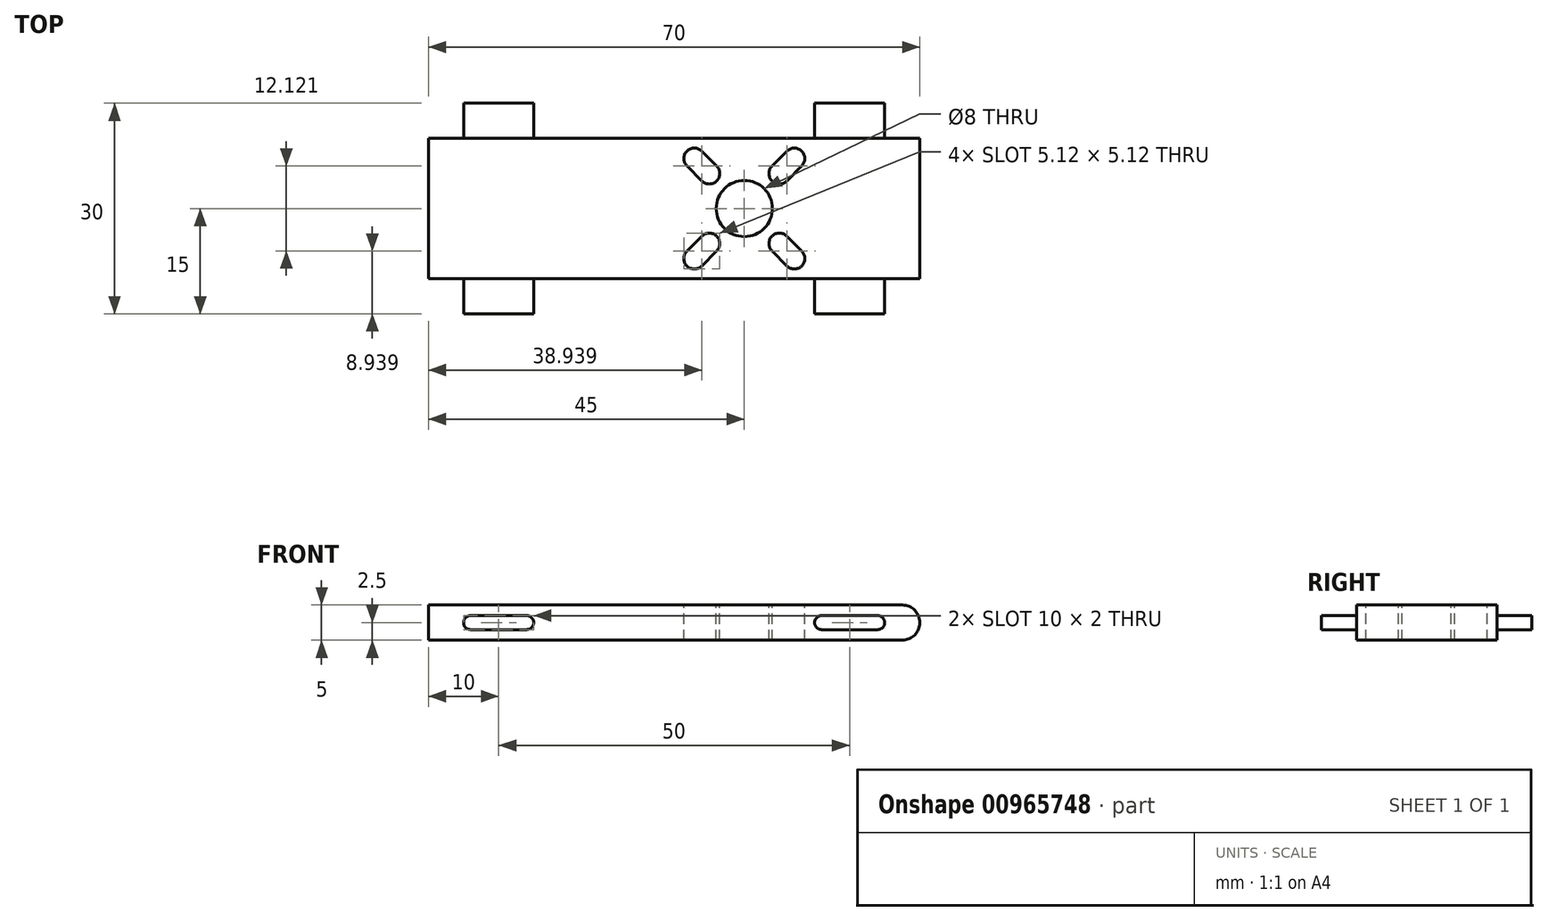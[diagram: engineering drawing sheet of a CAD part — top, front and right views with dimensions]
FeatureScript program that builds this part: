
annotation { "Feature Type Name" : "Feature", "Feature Type Description" : "" }
export const myFeature = defineFeature(function(context is Context, id is Id, definition is map)
    precondition{}
    {
        {
            var Q0;
            Q0=qCreatedBy(makeId("Top.planeOp"),FACE);
            var sketch = newSketch(context, id + "F0", { "sketchPlane" : qUnion([Q0])});
            skLineSegment(sketch, "E0.bottom", {"start": v(35, 10) * mm, "end": v(-35, 10) * mm});
            skLineSegment(sketch, "E0.top", {"start": v(35, -10) * mm, "end": v(-35, -10) * mm});
            skLineSegment(sketch, "E0.left", {"start": v(35, 10) * mm, "end": v(35, -10) * mm});
            skLineSegment(sketch, "E0.right", {"start": v(-35, 10) * mm, "end": v(-35, -10) * mm});
            skPoint(sketch, "E0.middle", {"position": v(0, 0) * mm});
            skSolve(sketch);
        }
        {
            var Q0;
            Q0=makeQuery(id+"F0.imprint","IMPRINT",FACE,{"disambiguationData":[TD([[makeQuery(id+"F0.imprint","IMPRINT",EDGE,{"derivedFrom":sQuery(id+"F0.wireOp",EDGE,"E0.bottom")}),1.0]])]});
            extrude(context, id + "F1", {"entities" : qUnion([Q0]), "depth" : 5 * mm, "offsetDistance" : 25 * mm});
        }
        {
            var Q0;
            Q0=makeQuery(id+"F1.opExtrude","SWEPT_FACE",FACE,{"disambiguationData":[OSD([sQuery(id+"F0.wireOp",EDGE,"E0.top")])]});
            var sketch = newSketch(context, id + "F2", { "sketchPlane" : qUnion([Q0])});
            skLineSegment(sketch, "E1.bottom", {"start": v(-20, 1.5) * mm, "end": v(-30, 1.5) * mm});
            skLineSegment(sketch, "E1.top", {"start": v(-20, 3.5) * mm, "end": v(-30, 3.5) * mm});
            skLineSegment(sketch, "E1.left", {"start": v(-20, 1.5) * mm, "end": v(-20, 3.5) * mm});
            skLineSegment(sketch, "E1.right", {"start": v(-30, 1.5) * mm, "end": v(-30, 3.5) * mm});
            skPoint(sketch, "E1.middle", {"position": v(-25, 2.5) * mm});
            skLineSegment(sketch, "E2.bottom", {"start": v(30, 1.5) * mm, "end": v(20, 1.5) * mm});
            skLineSegment(sketch, "E2.top", {"start": v(30, 3.5) * mm, "end": v(20, 3.5) * mm});
            skLineSegment(sketch, "E2.left", {"start": v(30, 1.5) * mm, "end": v(30, 3.5) * mm});
            skLineSegment(sketch, "E2.right", {"start": v(20, 1.5) * mm, "end": v(20, 3.5) * mm});
            skPoint(sketch, "E3.end.orphan", {"position": v(-35, 5) * mm});
            skPoint(sketch, "E4.start.orphan", {"position": v(35, 5) * mm});
            skSolve(sketch);
        }
        {
            var Q0;
            Q0 = qSketchRegion(id + "F2", true);
            extrude(context, id + "F3", {"entities" : qUnion([Q0]), "operationType" : NewBodyOperationType.ADD, "depth" : 5 * mm, "offsetDistance" : 25 * mm});
        }
        {
            var Q0;
            Q0=makeQuery(id+"F1.opExtrude","SWEPT_FACE",FACE,{"disambiguationData":[OSD([sQuery(id+"F0.wireOp",EDGE,"E0.bottom")])]});
            var sketch = newSketch(context, id + "F4", { "sketchPlane" : qUnion([Q0])});
            skLineSegment(sketch, "E5.bottom", {"start": v(-20, 3.5) * mm, "end": v(-30, 3.5) * mm});
            skLineSegment(sketch, "E5.top", {"start": v(-20, 1.5) * mm, "end": v(-30, 1.5) * mm});
            skLineSegment(sketch, "E5.left", {"start": v(-20, 3.5) * mm, "end": v(-20, 1.5) * mm});
            skLineSegment(sketch, "E5.right", {"start": v(-30, 3.5) * mm, "end": v(-30, 1.5) * mm});
            skPoint(sketch, "E5.middle", {"position": v(-25, 2.5) * mm});
            skLineSegment(sketch, "E6.bottom", {"start": v(30, 1.5) * mm, "end": v(20, 1.5) * mm});
            skLineSegment(sketch, "E6.top", {"start": v(30, 3.5) * mm, "end": v(20, 3.5) * mm});
            skLineSegment(sketch, "E6.left", {"start": v(30, 1.5) * mm, "end": v(30, 3.5) * mm});
            skLineSegment(sketch, "E6.right", {"start": v(20, 1.5) * mm, "end": v(20, 3.5) * mm});
            skPoint(sketch, "E6.middle", {"position": v(25, 2.5) * mm});
            skSolve(sketch);
        }
        {
            var Q0;
            Q0 = qSketchRegion(id + "F4", true);
            extrude(context, id + "F5", {"entities" : qUnion([Q0]), "operationType" : NewBodyOperationType.ADD, "depth" : 5 * mm, "offsetDistance" : 25 * mm});
        }
        {
            var Q0;
            Q0=makeQuery(id+"F5.opExtrude","SWEPT_EDGE",EDGE,{"disambiguationData":[OSD([sQuery(id+"F4.wireOp",EDGE,"E5.bottom"),sQuery(id+"F4.wireOp",EDGE,"E5.right")])]});
            var Q1;
            Q1=makeQuery(id+"F5.opExtrude","SWEPT_EDGE",EDGE,{"disambiguationData":[OSD([sQuery(id+"F4.wireOp",EDGE,"E5.top"),sQuery(id+"F4.wireOp",EDGE,"E5.right")])]});
            var Q2;
            Q2=makeQuery(id+"F5.opExtrude","SWEPT_EDGE",EDGE,{"disambiguationData":[OSD([sQuery(id+"F4.wireOp",EDGE,"E5.bottom"),sQuery(id+"F4.wireOp",EDGE,"E5.left")])]});
            var Q3;
            Q3=makeQuery(id+"F3.opExtrude","SWEPT_EDGE",EDGE,{"disambiguationData":[OSD([sQuery(id+"F2.wireOp",EDGE,"E2.top"),sQuery(id+"F2.wireOp",EDGE,"E2.left")])]});
            var Q4;
            Q4=makeQuery(id+"F3.opExtrude","SWEPT_EDGE",EDGE,{"disambiguationData":[OSD([sQuery(id+"F2.wireOp",EDGE,"E2.bottom"),sQuery(id+"F2.wireOp",EDGE,"E2.left")])]});
            var Q5;
            Q5=makeQuery(id+"F3.opExtrude","SWEPT_EDGE",EDGE,{"disambiguationData":[OSD([sQuery(id+"F2.wireOp",EDGE,"E2.top"),sQuery(id+"F2.wireOp",EDGE,"E2.right")])]});
            var Q6;
            Q6=makeQuery(id+"F5.opExtrude","SWEPT_EDGE",EDGE,{"disambiguationData":[OSD([sQuery(id+"F4.wireOp",EDGE,"E6.top"),sQuery(id+"F4.wireOp",EDGE,"E6.right")])]});
            var Q7;
            Q7=makeQuery(id+"F5.opExtrude","SWEPT_EDGE",EDGE,{"disambiguationData":[OSD([sQuery(id+"F4.wireOp",EDGE,"E6.bottom"),sQuery(id+"F4.wireOp",EDGE,"E6.right")])]});
            var Q8;
            Q8=makeQuery(id+"F3.opExtrude","SWEPT_EDGE",EDGE,{"disambiguationData":[OSD([sQuery(id+"F2.wireOp",EDGE,"E1.top"),sQuery(id+"F2.wireOp",EDGE,"E1.right")])]});
            var Q9;
            Q9=makeQuery(id+"F3.opExtrude","SWEPT_EDGE",EDGE,{"disambiguationData":[OSD([sQuery(id+"F2.wireOp",EDGE,"E1.top"),sQuery(id+"F2.wireOp",EDGE,"E1.left")])]});
            var Q10;
            Q10=makeQuery(id+"F3.opExtrude","SWEPT_EDGE",EDGE,{"disambiguationData":[OSD([sQuery(id+"F2.wireOp",EDGE,"E1.bottom"),sQuery(id+"F2.wireOp",EDGE,"E1.left")])]});
            var Q11;
            Q11=makeQuery(id+"F5.opExtrude","SWEPT_EDGE",EDGE,{"disambiguationData":[OSD([sQuery(id+"F4.wireOp",EDGE,"E6.top"),sQuery(id+"F4.wireOp",EDGE,"E6.left")])]});
            var Q12;
            Q12=makeQuery(id+"F5.opExtrude","SWEPT_EDGE",EDGE,{"disambiguationData":[OSD([sQuery(id+"F4.wireOp",EDGE,"E5.top"),sQuery(id+"F4.wireOp",EDGE,"E5.left")])]});
            var Q13;
            Q13=makeQuery(id+"F5.opExtrude","SWEPT_EDGE",EDGE,{"disambiguationData":[OSD([sQuery(id+"F4.wireOp",EDGE,"E6.bottom"),sQuery(id+"F4.wireOp",EDGE,"E6.left")])]});
            var Q14;
            Q14=makeQuery(id+"F3.opExtrude","SWEPT_EDGE",EDGE,{"disambiguationData":[OSD([sQuery(id+"F2.wireOp",EDGE,"E1.bottom"),sQuery(id+"F2.wireOp",EDGE,"E1.right")])]});
            var Q15;
            Q15=makeQuery(id+"F3.opExtrude","SWEPT_EDGE",EDGE,{"disambiguationData":[OSD([sQuery(id+"F2.wireOp",EDGE,"E2.bottom"),sQuery(id+"F2.wireOp",EDGE,"E2.right")])]});
            fillet(context, id + "F6", {"entities" : qUnion([Q0, Q1, Q2, Q3, Q4, Q5, Q6, Q7, Q8, Q9, Q10, Q11, Q12, Q13, Q14, Q15]), "radius" : 1 * mm, "tangentPropagation" : true, "allowEdgeOverflow" : false});
        }
        {
            var Q0;
            Q0=makeQuery(id+"F1.opExtrude","CAP_EDGE",EDGE,{"disambiguationData":[OSD([sQuery(id+"F0.wireOp",EDGE,"E0.left")])],"isStart":false});
            var Q1;
            Q1=makeQuery(id+"F1.opExtrude","CAP_EDGE",EDGE,{"disambiguationData":[OSD([sQuery(id+"F0.wireOp",EDGE,"E0.left")])],"isStart":true});
            fillet(context, id + "F7", {"entities" : qUnion([Q0, Q1]), "radius" : 2.5 * mm, "tangentPropagation" : true, "allowEdgeOverflow" : false});
        }
        {
            var Q0;
            Q0=makeQuery(id+"F1.opExtrude","CAP_FACE",FACE,{"disambiguationData":[OSD([sQuery(id+"F0.wireOp",EDGE,"E0.bottom"),sQuery(id+"F0.wireOp",EDGE,"E0.top"),sQuery(id+"F0.wireOp",EDGE,"E0.left"),sQuery(id+"F0.wireOp",EDGE,"E0.right")])],"isStart":false});
            var sketch = newSketch(context, id + "F8", { "sketchPlane" : qUnion([Q0])});
            skLineSegment(sketch, "E7", {"start": v(-35, 0) * mm, "end": v(32.5, 0) * mm});
            skLineSegment(sketch, "E8", {"start": v(0, 0) * mm, "end": v(0, 10) * mm});
            skLineSegment(sketch, "E9", {"start": v(0, 10) * mm, "end": v(20, 10) * mm});
            skLineSegment(sketch, "E10", {"start": v(20, 10) * mm, "end": v(20, -10) * mm});
            skLineSegment(sketch, "E11", {"start": v(20, -10) * mm, "end": v(0, -10) * mm});
            skCircle(sketch, "E12", {"center": v(10, 0) * mm, "radius": 4 * mm});
            skLineSegment(sketch, "E13", {"start": v(10, 0) * mm, "end": v(13.94, 3.94) * mm});
            skLineSegment(sketch, "E14", {"start": v(0, 10) * mm, "end": v(1.82, 8.18) * mm});
            skLineSegment(sketch, "E15", {"start": v(20, -10) * mm, "end": v(10, 0) * mm});
            skLineSegment(sketch, "E16", {"start": v(10, 0) * mm, "end": v(0, -10) * mm});
            skArc(sketch, "E17", {"start": v(13.94, 6.06) * mm, "mid": v(13.94, 3.94) * mm, "end": v(16.06, 3.94) * mm});
            skArc(sketch, "E18", {"start": v(18.18, 6.06) * mm, "mid": v(18.18, 8.18) * mm, "end": v(16.06, 8.18) * mm});
            skArc(sketch, "E19", {"start": v(6.06, -6.06) * mm, "mid": v(6.06, -3.94) * mm, "end": v(3.94, -3.94) * mm});
            skArc(sketch, "E20", {"start": v(1.82, -6.06) * mm, "mid": v(1.82, -8.18) * mm, "end": v(3.94, -8.18) * mm});
            skArc(sketch, "E21", {"start": v(3.94, 3.94) * mm, "mid": v(6.06, 3.94) * mm, "end": v(6.06, 6.06) * mm});
            skArc(sketch, "E22", {"start": v(3.94, 8.18) * mm, "mid": v(1.82, 8.18) * mm, "end": v(1.82, 6.06) * mm});
            skArc(sketch, "E23", {"start": v(16.06, -3.94) * mm, "mid": v(13.94, -3.94) * mm, "end": v(13.94, -6.06) * mm});
            skArc(sketch, "E24", {"start": v(16.06, -8.18) * mm, "mid": v(18.18, -8.18) * mm, "end": v(18.18, -6.06) * mm});
            skLineSegment(sketch, "E25", {"start": v(6.06, 6.06) * mm, "end": v(3.94, 8.18) * mm});
            skLineSegment(sketch, "E26", {"start": v(1.82, 6.06) * mm, "end": v(3.94, 3.94) * mm});
            skLineSegment(sketch, "E27.trimOffspring", {"start": v(6.06, 3.94) * mm, "end": v(10, 0) * mm});
            skLineSegment(sketch, "E28", {"start": v(13.94, 6.06) * mm, "end": v(16.06, 8.18) * mm});
            skLineSegment(sketch, "E29", {"start": v(16.06, 3.94) * mm, "end": v(18.18, 6.06) * mm});
            skLineSegment(sketch, "E30.trimOffspring", {"start": v(18.18, 8.18) * mm, "end": v(20, 10) * mm});
            skLineSegment(sketch, "E31", {"start": v(16.06, -3.94) * mm, "end": v(18.18, -6.06) * mm});
            skLineSegment(sketch, "E32", {"start": v(16.06, -8.18) * mm, "end": v(13.94, -6.06) * mm});
            skLineSegment(sketch, "E33", {"start": v(1.82, -6.06) * mm, "end": v(3.94, -3.94) * mm});
            skLineSegment(sketch, "E34", {"start": v(6.06, -6.06) * mm, "end": v(3.94, -8.18) * mm});
            skSolve(sketch);
        }
        {
            var Q0;
            {var subQ5=sQuery(id+"F8.wireOp",EDGE,"E34");Q0=makeQuery(id+"F8.imprint","IMPRINT",FACE,{"disambiguationData":[TD([[makeQuery(id+"F8.imprint","IMPRINT",EDGE,{"derivedFrom":subQ5}),-1.0]])]});}
            var Q1;
            {var subQ5=sQuery(id+"F8.wireOp",EDGE,"E33");Q1=makeQuery(id+"F8.imprint","IMPRINT",FACE,{"disambiguationData":[TD([[makeQuery(id+"F8.imprint","IMPRINT",EDGE,{"derivedFrom":subQ5}),-1.0]])]});}
            var Q2;
            {var subQ1=sQuery(id+"F8.wireOp",EDGE,"E7");var subQ3=sQuery(id+"F8.wireOp",EDGE,"E12");var subQ4=makeQuery(id+"F8.imprint","INTERSECT",VERTEX,{"disambiguationData":[OD(0.0)],"derivedFrom":[subQ1,subQ3]});Q2=makeQuery(id+"F8.imprint","IMPRINT",FACE,{"disambiguationData":[TD([[makeQuery(id+"F8.imprint","IMPRINT",EDGE,{"disambiguationData":[TD([[subQ4,1.0]])],"derivedFrom":subQ3}),1.0]])]});}
            var Q3;
            {var subQ1=sQuery(id+"F8.wireOp",EDGE,"E7");var subQ3=sQuery(id+"F8.wireOp",EDGE,"E12");var subQ4=makeQuery(id+"F8.imprint","INTERSECT",VERTEX,{"disambiguationData":[OD(0.0)],"derivedFrom":[subQ1,subQ3]});Q3=makeQuery(id+"F8.imprint","IMPRINT",FACE,{"disambiguationData":[TD([[makeQuery(id+"F8.imprint","IMPRINT",EDGE,{"disambiguationData":[TD([[subQ4,-1.0]])],"derivedFrom":subQ3}),1.0]])]});}
            var Q4;
            {var subQ0=sQuery(id+"F8.wireOp",EDGE,"E16");var subQ1=sQuery(id+"F8.wireOp",EDGE,"E12");var subQ2=makeQuery(id+"F8.imprint","INTERSECT",VERTEX,{"derivedFrom":[subQ1,subQ0]});Q4=makeQuery(id+"F8.imprint","IMPRINT",FACE,{"disambiguationData":[TD([[makeQuery(id+"F8.imprint","IMPRINT",EDGE,{"disambiguationData":[TD([[subQ2,-1.0]])],"derivedFrom":subQ1}),1.0]])]});}
            var Q5;
            {var subQ5=sQuery(id+"F8.wireOp",EDGE,"E31");Q5=makeQuery(id+"F8.imprint","IMPRINT",FACE,{"disambiguationData":[TD([[makeQuery(id+"F8.imprint","IMPRINT",EDGE,{"derivedFrom":subQ5}),-1.0]])]});}
            var Q6;
            {var subQ5=sQuery(id+"F8.wireOp",EDGE,"E32");Q6=makeQuery(id+"F8.imprint","IMPRINT",FACE,{"disambiguationData":[TD([[makeQuery(id+"F8.imprint","IMPRINT",EDGE,{"derivedFrom":subQ5}),-1.0]])]});}
            var Q7;
            {var subQ0=sQuery(id+"F8.wireOp",EDGE,"E28");Q7=makeQuery(id+"F8.imprint","IMPRINT",FACE,{"disambiguationData":[TD([[makeQuery(id+"F8.imprint","IMPRINT",EDGE,{"derivedFrom":subQ0}),-1.0]])]});}
            var Q8;
            {var subQ3=sQuery(id+"F8.wireOp",EDGE,"E25");Q8=makeQuery(id+"F8.imprint","IMPRINT",FACE,{"disambiguationData":[TD([[makeQuery(id+"F8.imprint","IMPRINT",EDGE,{"derivedFrom":subQ3}),1.0]])]});}
            var Q9;
            {var subQ0=sQuery(id+"F8.wireOp",EDGE,"E13");var subQ1=sQuery(id+"F8.wireOp",EDGE,"E12");var subQ2=makeQuery(id+"F8.imprint","INTERSECT",VERTEX,{"derivedFrom":[subQ1,subQ0]});Q9=makeQuery(id+"F8.imprint","IMPRINT",FACE,{"disambiguationData":[TD([[makeQuery(id+"F8.imprint","IMPRINT",EDGE,{"disambiguationData":[TD([[subQ2,-1.0]])],"derivedFrom":subQ1}),1.0]])]});}
            var Q10;
            {var subQ1=sQuery(id+"F8.wireOp",EDGE,"E7");var subQ3=sQuery(id+"F8.wireOp",EDGE,"E12");var subQ4=makeQuery(id+"F8.imprint","INTERSECT",VERTEX,{"disambiguationData":[OD(1.0)],"derivedFrom":[subQ1,subQ3]});Q10=makeQuery(id+"F8.imprint","IMPRINT",FACE,{"disambiguationData":[TD([[makeQuery(id+"F8.imprint","IMPRINT",EDGE,{"disambiguationData":[TD([[subQ4,-1.0]])],"derivedFrom":subQ3}),1.0]])]});}
            var Q11;
            {var subQ1=sQuery(id+"F8.wireOp",EDGE,"E7");var subQ3=sQuery(id+"F8.wireOp",EDGE,"E12");var subQ4=makeQuery(id+"F8.imprint","INTERSECT",VERTEX,{"disambiguationData":[OD(1.0)],"derivedFrom":[subQ1,subQ3]});Q11=makeQuery(id+"F8.imprint","IMPRINT",FACE,{"disambiguationData":[TD([[makeQuery(id+"F8.imprint","IMPRINT",EDGE,{"disambiguationData":[TD([[subQ4,1.0]])],"derivedFrom":subQ3}),1.0]])]});}
            extrude(context, id + "F9", {"entities" : qUnion([Q0, Q1, Q2, Q3, Q4, Q5, Q6, Q7, Q8, Q9, Q10, Q11]), "operationType" : NewBodyOperationType.REMOVE, "oppositeDirection" : true, "depth" : 5 * mm, "offsetDistance" : 25 * mm});
        }
    });
